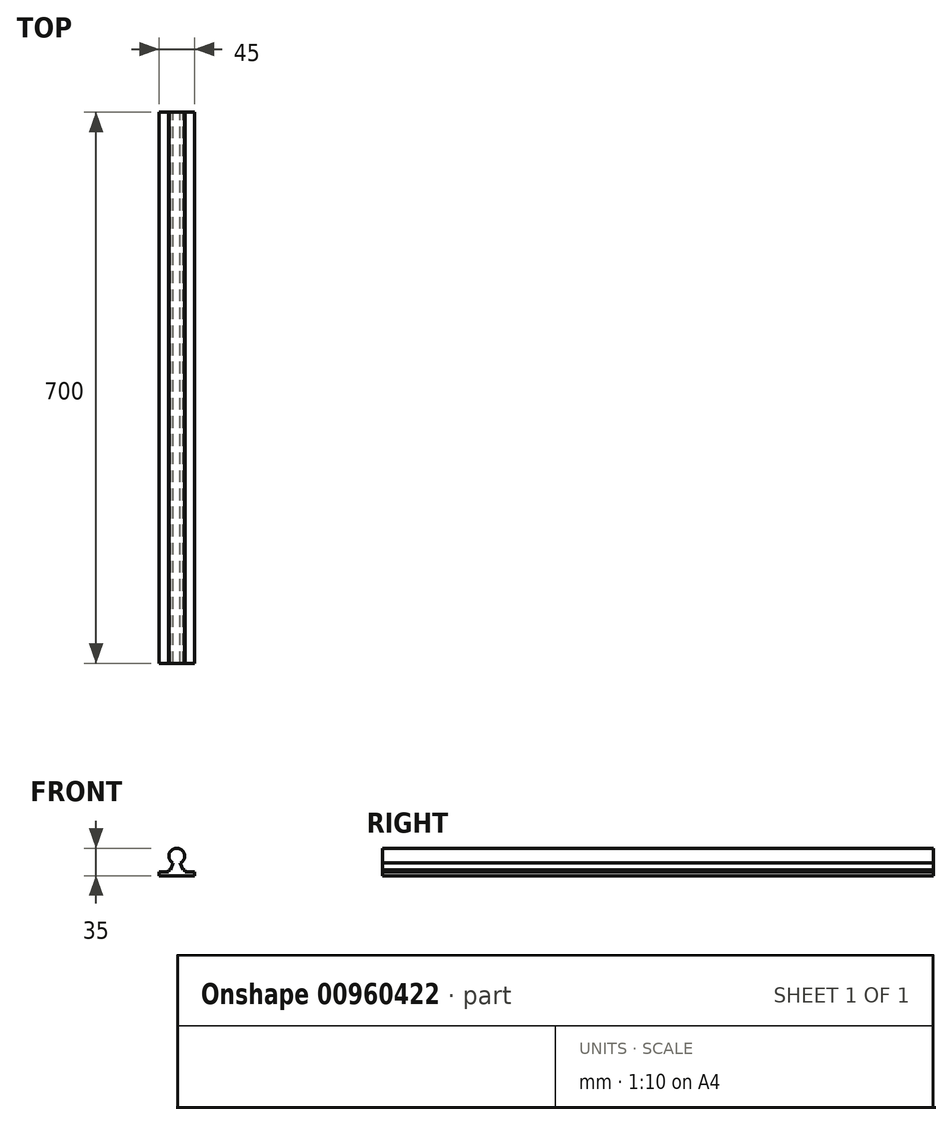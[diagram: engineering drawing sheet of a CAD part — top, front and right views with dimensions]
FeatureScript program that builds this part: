
annotation { "Feature Type Name" : "Feature", "Feature Type Description" : "" }
export const myFeature = defineFeature(function(context is Context, id is Id, definition is map)
    precondition{}
    {
        {
            var Q0;
            Q0=qCreatedBy(makeId("Front.planeOp"),FACE);
            var sketch = newSketch(context, id + "F0", { "sketchPlane" : qUnion([Q0])});
            skCircle(sketch, "E0", {"center": v(0, 0) * mm, "radius": 10 * mm});
            skLineSegment(sketch, "E1", {"start": v(-22.5, -25) * mm, "end": v(22.5, -25) * mm});
            skPoint(sketch, "E2", {"position": v(0, -25) * mm});
            skLineSegment(sketch, "E3", {"start": v(-22.5, -25) * mm, "end": v(-22.5, -20) * mm});
            skLineSegment(sketch, "E4", {"start": v(-22.5, -20) * mm, "end": v(-10.5, -20) * mm});
            skLineSegment(sketch, "E5", {"start": v(-10.5, -20) * mm, "end": v(-10.5, -17.5) * mm});
            skLineSegment(sketch, "E6", {"start": v(-10.5, -17.5) * mm, "end": v(-8, -17.5) * mm});
            skLineSegment(sketch, "E7", {"start": v(-8, -17.5) * mm, "end": v(-4.5, -8.93) * mm});
            skLineSegment(sketch, "E8", {"start": v(0, -29.05) * mm, "end": v(0, 13.28) * mm, "construction": true});
            skLineSegment(sketch, "E9.MirrorCS", {"start": v(8, -17.5) * mm, "end": v(4.5, -8.93) * mm});
            skLineSegment(sketch, "E10.MirrorCS", {"start": v(10.5, -17.5) * mm, "end": v(8, -17.5) * mm});
            skLineSegment(sketch, "E11.MirrorCS", {"start": v(10.5, -20) * mm, "end": v(10.5, -17.5) * mm});
            skLineSegment(sketch, "E12.MirrorCS", {"start": v(22.5, -20) * mm, "end": v(10.5, -20) * mm});
            skLineSegment(sketch, "E13.MirrorCS", {"start": v(22.5, -25) * mm, "end": v(22.5, -20) * mm});
            skSolve(sketch);
        }
        {
            var Q0;
            Q0=qSketchRegion(id+"F0",true);
            extrude(context, id + "F1", {"entities" : qUnion([Q0]), "depth" : 700 * mm, "offsetDistance" : 25 * mm});
        }
    });
